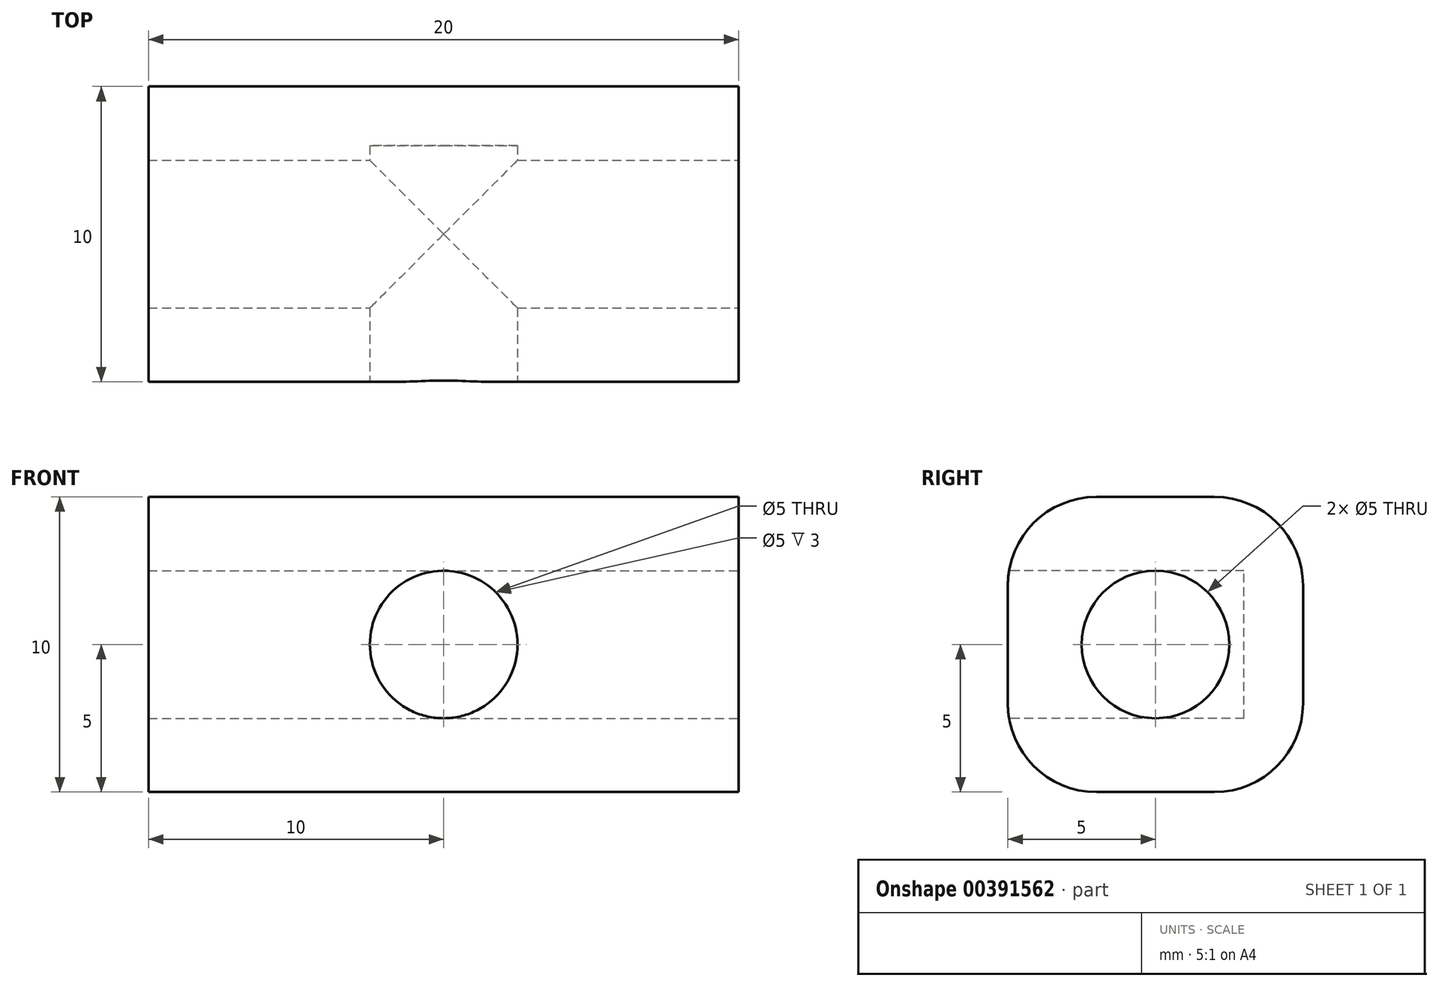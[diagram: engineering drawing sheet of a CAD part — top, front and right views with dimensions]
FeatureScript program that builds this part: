
annotation { "Feature Type Name" : "Feature", "Feature Type Description" : "" }
export const myFeature = defineFeature(function(context is Context, id is Id, definition is map)
    precondition{}
    {
        {
            var Q0;
            Q0=qCreatedBy(makeId("Front.planeOp"),FACE);
            var sketch = newSketch(context, id + "F0", { "sketchPlane" : qUnion([Q0])});
            skLineSegment(sketch, "E0.bottom", {"start": v(-10, 0) * mm, "end": v(10, 0) * mm});
            skLineSegment(sketch, "E0.top", {"start": v(-10, 10) * mm, "end": v(10, 10) * mm});
            skLineSegment(sketch, "E0.left", {"start": v(-10, 0) * mm, "end": v(-10, 10) * mm});
            skLineSegment(sketch, "E0.right", {"start": v(10, 0) * mm, "end": v(10, 10) * mm});
            skSolve(sketch);
        }
        {
            var Q0;
            Q0 = qSketchRegion(id + "F0", true);
            extrude(context, id + "F1", {"entities" : qUnion([Q0]), "depth" : 10 * mm});
        }
        {
            var Q0;
            Q0=makeQuery(id+"F1.opExtrude","CAP_FACE",FACE,{"disambiguationData":[OSD([sQuery(id+"F0.wireOp",EDGE,"E0.bottom"),sQuery(id+"F0.wireOp",EDGE,"E0.top"),sQuery(id+"F0.wireOp",EDGE,"E0.left"),sQuery(id+"F0.wireOp",EDGE,"E0.right")])],"isStart":false});
            var sketch = newSketch(context, id + "F2", { "sketchPlane" : qUnion([Q0])});
            skCircle(sketch, "E1", {"center": v(0, 5) * mm, "radius": 2.5 * mm});
            skLineSegment(sketch, "E2", {"start": v(0, 10) * mm, "end": v(0, 0) * mm, "construction": true});
            skSolve(sketch);
        }
        {
            var Q0;
            Q0 = qSketchRegion(id + "F2", true);
            extrude(context, id + "F3", {"entities" : qUnion([Q0]), "operationType" : NewBodyOperationType.REMOVE, "oppositeDirection" : true, "depth" : 8 * mm});
        }
        {
            var Q0;
            Q0=qCreatedBy(makeId("Right.planeOp"),FACE);
            var sketch = newSketch(context, id + "F4", { "sketchPlane" : qUnion([Q0])});
            skCircle(sketch, "E3", {"center": v(-5, 5) * mm, "radius": 2.5 * mm});
            skLineSegment(sketch, "E4", {"start": v(-10, 10) * mm, "end": v(0, 0) * mm, "construction": true});
            skSolve(sketch);
        }
        {
            var Q0;
            Q0 = qSketchRegion(id + "F4", true);
            extrude(context, id + "F5", {"entities" : qUnion([Q0]), "operationType" : NewBodyOperationType.REMOVE, "endBound" : BoundingType.THROUGH_ALL, "oppositeDirection" : true, "depth" : 25 * mm, "hasSecondDirection" : true, "secondDirectionBound" : SecondDirectionBoundingType.THROUGH_ALL, "secondDirectionOppositeDirection" : false, "secondDirectionDepth" : 25 * mm});
        }
        {
            var Q0;
            Q0=makeQuery(id+"F1.opExtrude","CAP_EDGE",EDGE,{"disambiguationData":[OSD([sQuery(id+"F0.wireOp",EDGE,"E0.top")])],"isStart":true});
            var Q1;
            Q1=makeQuery(id+"F1.opExtrude","CAP_EDGE",EDGE,{"disambiguationData":[OSD([sQuery(id+"F0.wireOp",EDGE,"E0.top")])],"isStart":false});
            var Q2;
            Q2=makeQuery(id+"F1.opExtrude","CAP_EDGE",EDGE,{"disambiguationData":[OSD([sQuery(id+"F0.wireOp",EDGE,"E0.bottom")])],"isStart":false});
            var Q3;
            Q3=makeQuery(id+"F1.opExtrude","CAP_EDGE",EDGE,{"disambiguationData":[OSD([sQuery(id+"F0.wireOp",EDGE,"E0.bottom")])],"isStart":true});
            fillet(context, id + "F6", {"entities" : qUnion([Q0, Q1, Q2, Q3]), "radius" : 3 * mm, "tangentPropagation" : true, "allowEdgeOverflow" : false});
        }
    });
